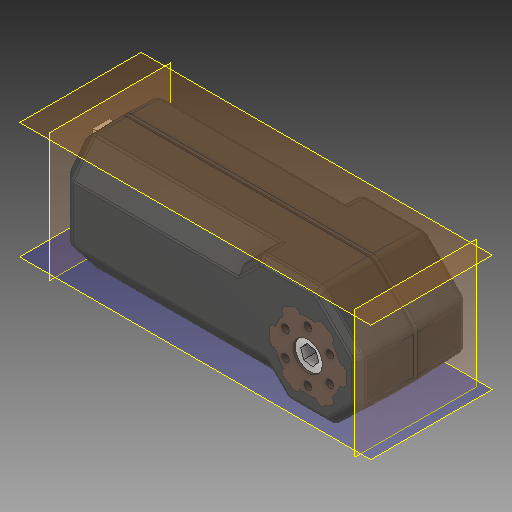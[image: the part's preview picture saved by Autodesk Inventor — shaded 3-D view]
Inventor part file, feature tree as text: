
AUTODESK INVENTOR PART (.ipt)
format: ipt  version: 2017 (Build 210142000, 142)  size: 4,255,744 bytes
history: native  units: in
note: dims shown in document units (in); Inventor stores cm internally (conversion verified against a paired STEP export)
features: other x10, plane x4
ambient origin geometry x8: Origin, YZ Plane, XZ Plane, XY Plane, X Axis, Y Axis, Z Axis, Center Point
bodies: Solid1 (feature_tree), Solid2 (feature_tree), Solid3 (feature_tree), Solid4 (feature_tree), Solid5 (feature_tree), Solid6 (feature_tree), Solid7 (feature_tree), Solid8 (feature_tree)
feature tree (14):
  other  "REV-41-1300HexMotor.ipt"
  other  "Solid1::REV-41-1300HexMotor.ipt"
  other  "Solid2::REV-41-1300HexMotor.ipt"
  other  "Solid3::REV-41-1300HexMotor.ipt"
  other  "Solid4::REV-41-1300HexMotor.ipt"
  other  "Solid5::REV-41-1300HexMotor.ipt"
  other  "Solid6::REV-41-1300HexMotor.ipt"
  other  "Solid7::REV-41-1300HexMotor.ipt"
  other  "Solid8::REV-41-1300HexMotor.ipt"
  other  "TaggingFeature1"
  plane  "Work Plane1"
  plane  "Work Plane2"
  plane  "Work Plane3"
  plane  "Work Plane4"
